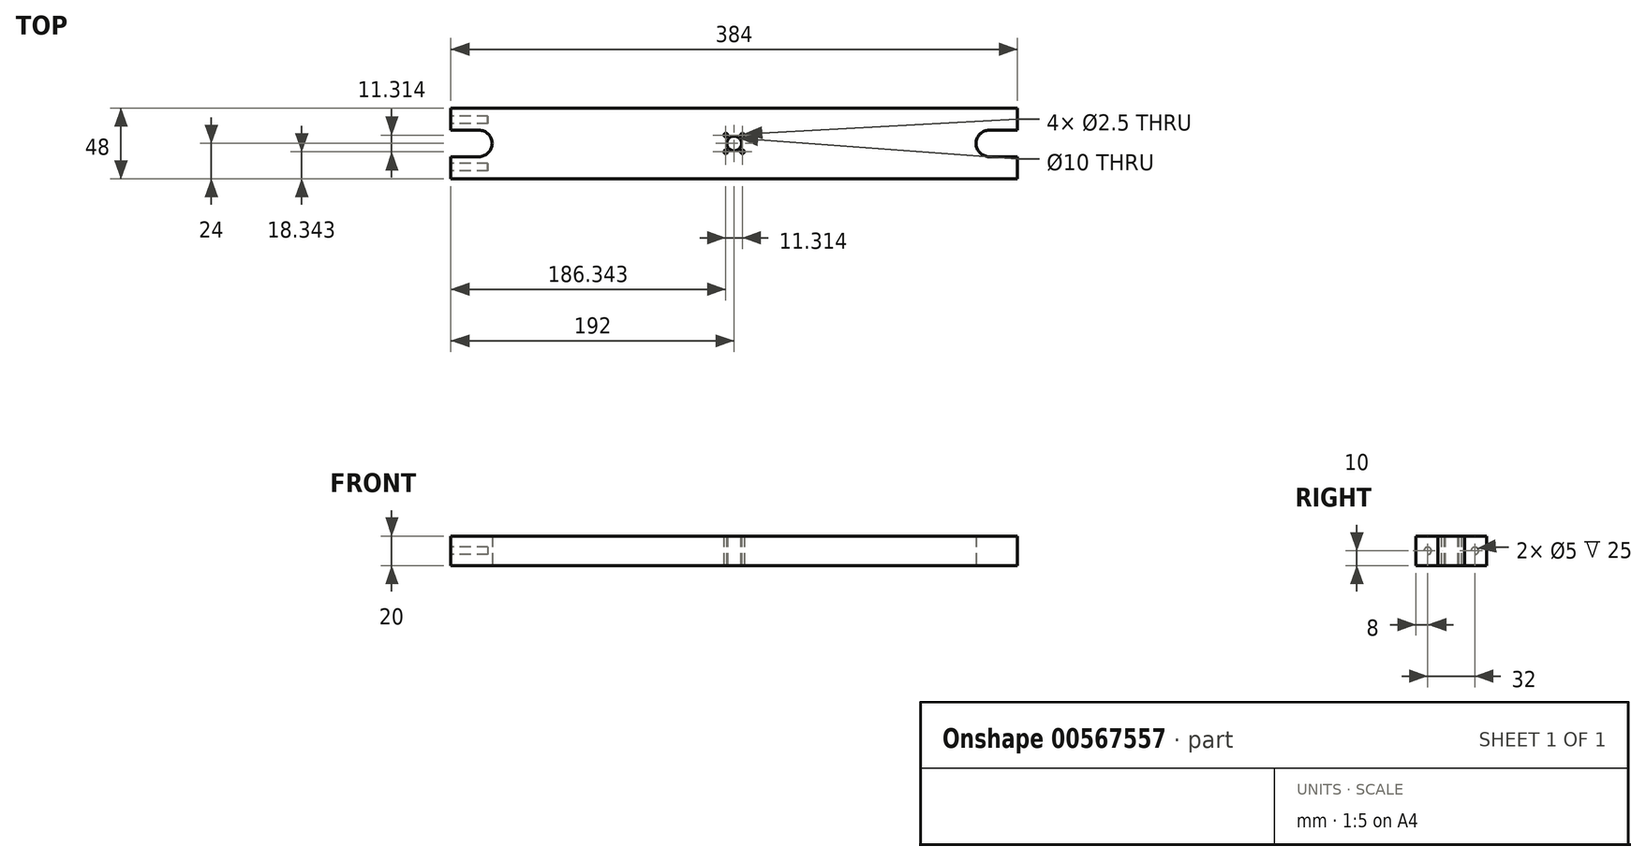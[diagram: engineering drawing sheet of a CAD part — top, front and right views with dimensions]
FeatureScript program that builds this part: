
annotation { "Feature Type Name" : "Feature", "Feature Type Description" : "" }
export const myFeature = defineFeature(function(context is Context, id is Id, definition is map)
    precondition{}
    {
        {
            var Q0;
            Q0=qCreatedBy(makeId("Top.planeOp"),FACE);
            var sketch = newSketch(context, id + "F0", { "sketchPlane" : qUnion([Q0])});
            skLineSegment(sketch, "E0.bottom", {"start": v(192, -24) * mm, "end": v(-192, -24) * mm});
            skLineSegment(sketch, "E0.top", {"start": v(192, 24) * mm, "end": v(-192, 24) * mm});
            skLineSegment(sketch, "E0.left", {"start": v(192, -24) * mm, "end": v(192, -9) * mm});
            skLineSegment(sketch, "E0.right", {"start": v(-192, -24) * mm, "end": v(-192, -9) * mm});
            skPoint(sketch, "E0.middle", {"position": v(0, 0) * mm});
            skArc(sketch, "E1", {"start": v(-173, -9) * mm, "mid": v(-164, 0) * mm, "end": v(-173, 9) * mm});
            skLineSegment(sketch, "E2", {"start": v(-173, 9) * mm, "end": v(-192, 9) * mm});
            skLineSegment(sketch, "E3", {"start": v(-173, -9) * mm, "end": v(-192, -9) * mm});
            skLineSegment(sketch, "E4.trimOffspring", {"start": v(-192, 9) * mm, "end": v(-192, 24) * mm});
            skLineSegment(sketch, "E5.MirrorCS", {"start": v(173, 9) * mm, "end": v(192, 9) * mm});
            skArc(sketch, "E6.MirrorCS", {"start": v(173, -9) * mm, "mid": v(164, 0) * mm, "end": v(173, 9) * mm});
            skLineSegment(sketch, "E7.MirrorCS", {"start": v(173, -9) * mm, "end": v(192, -9) * mm});
            skLineSegment(sketch, "E8.trimOffspring", {"start": v(192, 9) * mm, "end": v(192, 24) * mm});
            skSolve(sketch);
        }
        {
            var Q0;
            Q0=makeQuery(id+"F0.imprint","IMPRINT",FACE,{"disambiguationData":[TD([[makeQuery(id+"F0.imprint","IMPRINT",EDGE,{"derivedFrom":sQuery(id+"F0.wireOp",EDGE,"E0.bottom")}),-1.0]])]});
            extrude(context, id + "F1", {"entities" : qUnion([Q0]), "depth" : 20 * mm, "offsetDistance" : 25 * mm});
        }
        {
            var Q0;
            Q0=makeQuery(id+"F1.opExtrude","SWEPT_FACE",FACE,{"disambiguationData":[OSD([sQuery(id+"F0.wireOp",EDGE,"E0.right")])]});
            var sketch = newSketch(context, id + "F2", { "sketchPlane" : qUnion([Q0])});
            skCircle(sketch, "E9", {"center": v(16, 10) * mm, "radius": 2.5 * mm});
            skPoint(sketch, "E9.centerSnap0", {"position": v(24, 10) * mm});
            skCircle(sketch, "E10", {"center": v(-16, 10) * mm, "radius": 2.5 * mm});
            skSolve(sketch);
        }
        {
            var Q0;
            Q0=makeQuery(id+"F2.imprint","IMPRINT",FACE,{"disambiguationData":[TD([[makeQuery(id+"F2.imprint","IMPRINT",EDGE,{"derivedFrom":sQuery(id+"F2.wireOp",EDGE,"E10")}),1.0]])]});
            var Q1;
            Q1=makeQuery(id+"F2.imprint","IMPRINT",FACE,{"disambiguationData":[TD([[makeQuery(id+"F2.imprint","IMPRINT",EDGE,{"derivedFrom":sQuery(id+"F2.wireOp",EDGE,"E9")}),1.0]])]});
            extrude(context, id + "F3", {"entities" : qUnion([Q0, Q1]), "operationType" : NewBodyOperationType.REMOVE, "oppositeDirection" : true, "depth" : 25 * mm, "offsetDistance" : 25 * mm});
        }
        {
            var Q0;
            Q0=makeQuery(id+"F1.opExtrude","CAP_FACE",FACE,{"disambiguationData":[OSD([sQuery(id+"F0.wireOp",EDGE,"E0.bottom"),sQuery(id+"F0.wireOp",EDGE,"E0.top"),sQuery(id+"F0.wireOp",EDGE,"E0.left"),sQuery(id+"F0.wireOp",EDGE,"E0.right"),sQuery(id+"F0.wireOp",EDGE,"E1"),sQuery(id+"F0.wireOp",EDGE,"E2"),sQuery(id+"F0.wireOp",EDGE,"E3"),sQuery(id+"F0.wireOp",EDGE,"E4.trimOffspring"),sQuery(id+"F0.wireOp",EDGE,"E5.MirrorCS"),sQuery(id+"F0.wireOp",EDGE,"E6.MirrorCS"),sQuery(id+"F0.wireOp",EDGE,"E7.MirrorCS"),sQuery(id+"F0.wireOp",EDGE,"E8.trimOffspring")])],"isStart":true});
            var sketch = newSketch(context, id + "F4", { "sketchPlane" : qUnion([Q0])});
            skCircle(sketch, "E11", {"center": v(0, 0) * mm, "radius": 5 * mm});
            skCircle(sketch, "E12", {"center": v(0, 0) * mm, "radius": 15 * mm, "construction": true});
            skCircle(sketch, "E13", {"center": v(0, 0) * mm, "radius": 8 * mm, "construction": true});
            skLineSegment(sketch, "E14.bottom", {"start": v(5.66, -5.66) * mm, "end": v(-5.66, -5.66) * mm, "construction": true});
            skLineSegment(sketch, "E14.top", {"start": v(5.66, 5.66) * mm, "end": v(-5.66, 5.66) * mm, "construction": true});
            skLineSegment(sketch, "E14.left", {"start": v(5.66, -5.66) * mm, "end": v(5.66, 5.66) * mm, "construction": true});
            skLineSegment(sketch, "E14.right", {"start": v(-5.66, -5.66) * mm, "end": v(-5.66, 5.66) * mm, "construction": true});
            skCircle(sketch, "E15", {"center": v(-5.66, 5.66) * mm, "radius": 1.25 * mm});
            skCircle(sketch, "E16", {"center": v(-5.66, -5.66) * mm, "radius": 1.25 * mm});
            skCircle(sketch, "E17", {"center": v(5.66, -5.66) * mm, "radius": 1.25 * mm});
            skCircle(sketch, "E18", {"center": v(5.66, 5.66) * mm, "radius": 1.25 * mm});
            skSolve(sketch);
        }
        {
            var Q0;
            Q0 = qSketchRegion(id + "F4", true);
            extrude(context, id + "F5", {"entities" : qUnion([Q0]), "operationType" : NewBodyOperationType.REMOVE, "oppositeDirection" : true, "depth" : 25 * mm, "offsetDistance" : 25 * mm});
        }
    });
